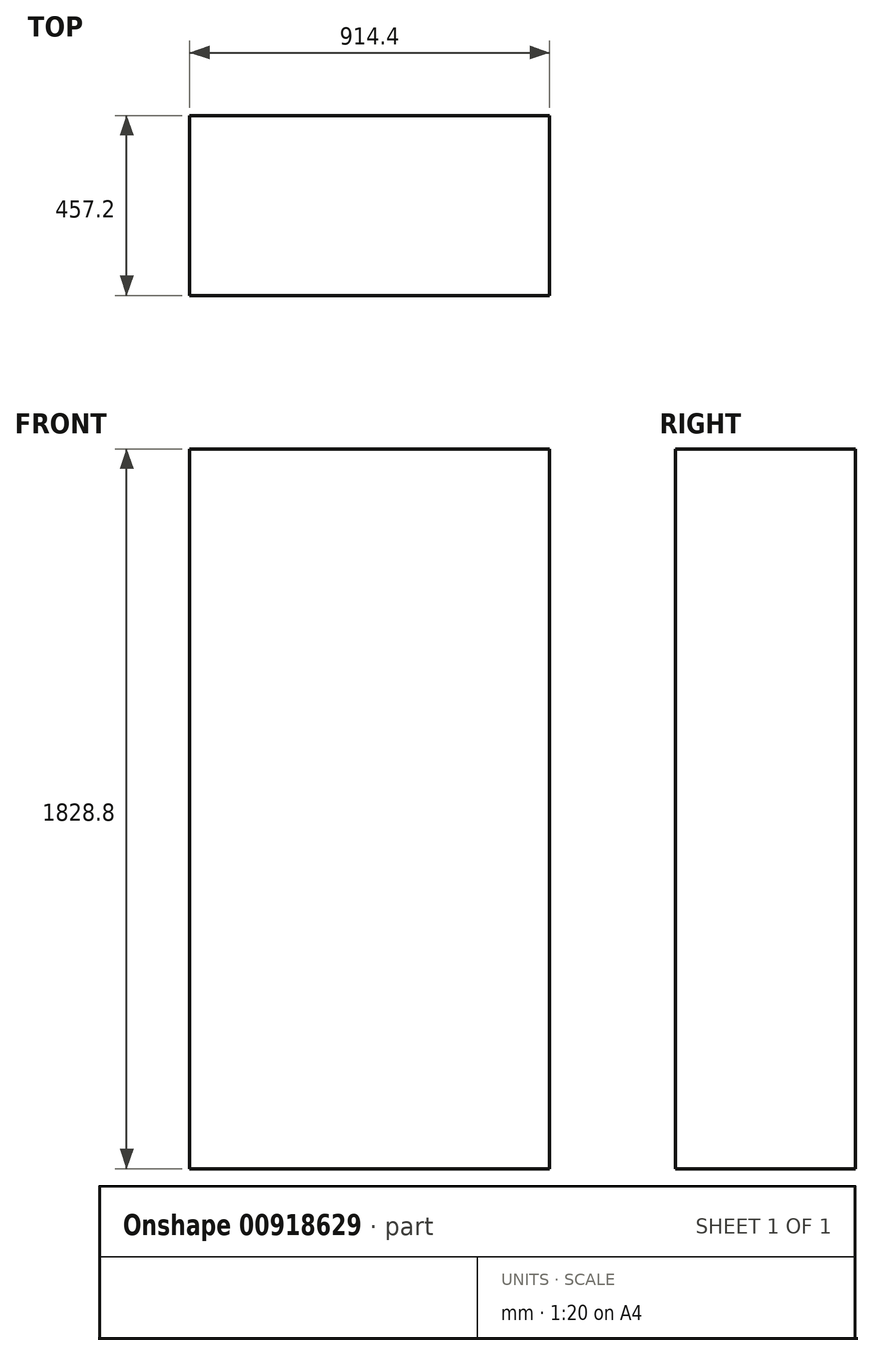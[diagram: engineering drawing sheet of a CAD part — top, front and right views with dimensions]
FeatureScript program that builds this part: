
annotation { "Feature Type Name" : "Feature", "Feature Type Description" : "" }
export const myFeature = defineFeature(function(context is Context, id is Id, definition is map)
    precondition{}
    {
        {
            var Q0;
            Q0=qCreatedBy(makeId("Front.planeOp"),FACE);
            var sketch = newSketch(context, id + "F0", { "sketchPlane" : qUnion([Q0])});
            skLineSegment(sketch, "E0.bottom", {"start": v(-457.2, 914.4) * mm, "end": v(457.2, 914.4) * mm});
            skLineSegment(sketch, "E0.top", {"start": v(-457.2, -914.4) * mm, "end": v(457.2, -914.4) * mm});
            skLineSegment(sketch, "E0.left", {"start": v(-457.2, 914.4) * mm, "end": v(-457.2, -914.4) * mm});
            skLineSegment(sketch, "E0.right", {"start": v(457.2, 914.4) * mm, "end": v(457.2, -914.4) * mm});
            skLineSegment(sketch, "E1", {"start": v(-457.2, 914.4) * mm, "end": v(457.2, -914.4) * mm, "construction": true});
            skSolve(sketch);
        }
        {
            var Q0;
            Q0=makeQuery(id+"F0.imprint","IMPRINT",FACE,{"disambiguationData":[TD([[makeQuery(id+"F0.imprint","IMPRINT",EDGE,{"derivedFrom":sQuery(id+"F0.wireOp",EDGE,"E0.bottom")}),-1.0]])]});
            extrude(context, id + "F1", {"entities" : qUnion([Q0]), "depth" : 457.2 * mm, "offsetDistance" : 25.4 * mm});
        }
    });
